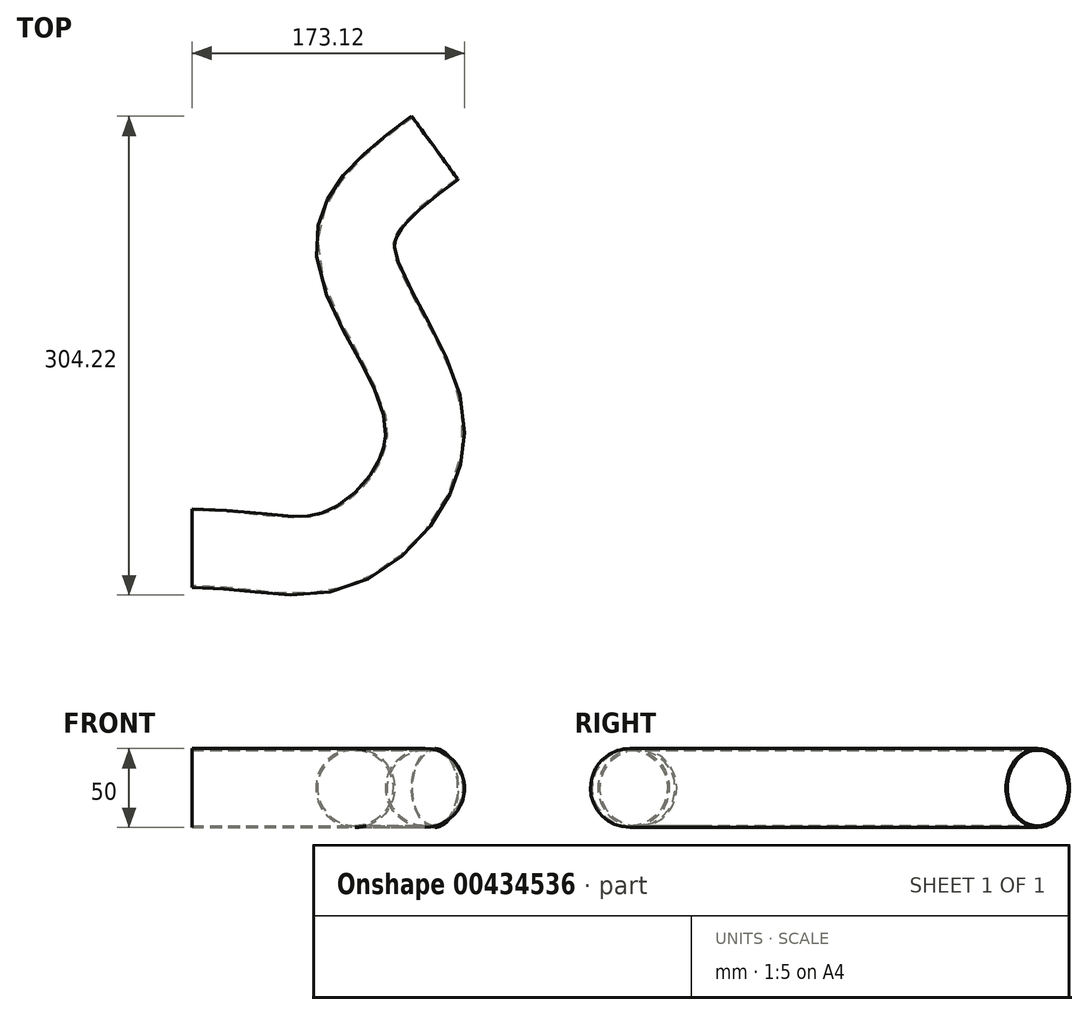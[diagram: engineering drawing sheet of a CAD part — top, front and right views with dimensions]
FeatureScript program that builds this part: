
annotation { "Feature Type Name" : "Feature", "Feature Type Description" : "" }
export const myFeature = defineFeature(function(context is Context, id is Id, definition is map)
    precondition{}
    {
        {
            var Q0;
            Q0=qCreatedBy(makeId("Right.planeOp"),FACE);
            var sketch = newSketch(context, id + "F0", { "sketchPlane" : qUnion([Q0])});
            skCircle(sketch, "E0", {"center": v(0, 0) * mm, "radius": 25 * mm});
            skSolve(sketch);
        }
        {
            var Q0;
            Q0=qCreatedBy(makeId("Top.planeOp"),FACE);
            var sketch = newSketch(context, id + "F1", { "sketchPlane" : qUnion([Q0])});
            skFitSpline(sketch, "E1", {"points": [v(0, 0) * mm, v(94.37, 0) * mm, v(148.04, 77.46) * mm, v(103.71, 190.55) * mm, v(154.32, 254.28) * mm], "startDerivative": vector(510.85, 0) * mm, "endDerivative": vector(337.27, 247.22) * mm});
            skSolve(sketch);
        }
        {
            var Q0;
            Q0=makeQuery(id+"F0.imprint","IMPRINT",FACE,{"disambiguationData":[TD([[makeQuery(id+"F0.imprint","IMPRINT",EDGE,{"derivedFrom":sQuery(id+"F0.wireOp",EDGE,"E0")}),1.0]])]});
            var Q1;
            Q1=sQuery(id+"F1.wireOp",EDGE,"E1");
            sweep(context, id + "F2", {"profiles" : qUnion([Q0]), "path" : qUnion([Q1])});
        }
        {
            var Q0;
            Q0=makeQuery(id+"F2.opSweep","CAP_FACE",FACE,{"disambiguationData":[OSD([sQuery(id+"F0.wireOp",EDGE,"E0"),sQuery(id+"F1.wireOp",VERTEX,"E1.end")])],"isStart":false});
            var Q1;
            Q1=makeQuery(id+"F2.opSweep","CAP_FACE",FACE,{"disambiguationData":[OSD([sQuery(id+"F0.wireOp",EDGE,"E0"),sQuery(id+"F1.wireOp",VERTEX,"E1.start")])],"isStart":true});
            var Q2;
            Q2=makeQuery(id+"F2.opSweep","SWEPT_BODY",BODY,{"disambiguationData":[OSD([sQuery(id+"F0.wireOp",EDGE,"E0"),sQuery(id+"F1.wireOp",EDGE,"E1")])]});
            shell(context, id + "F3", {"entities" : qUnion([Q0, Q1]), "parts" : qUnion([Q2]), "thickness" : 1 * mm});
        }
    });
